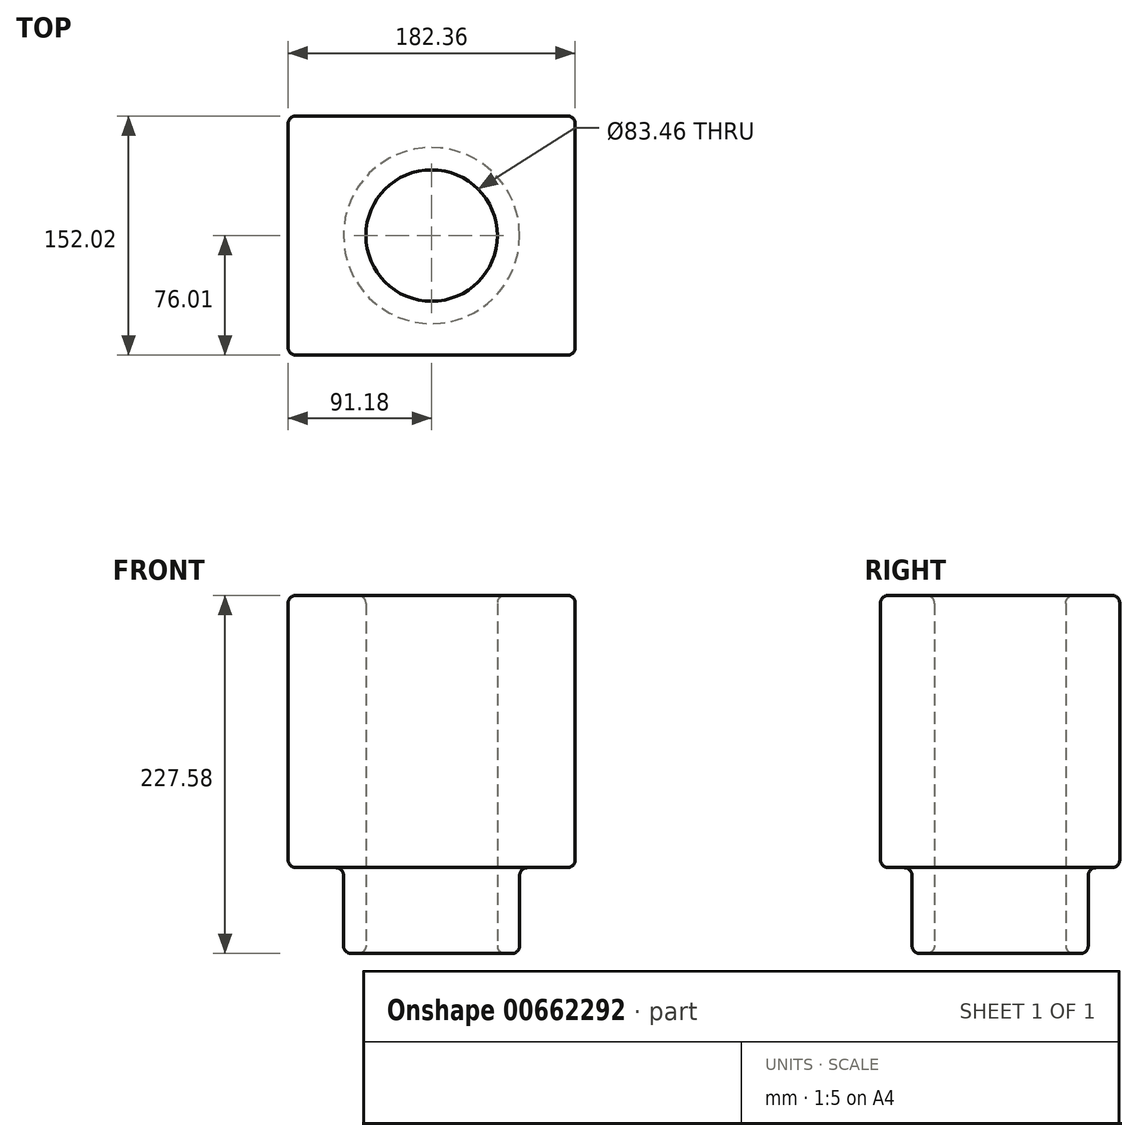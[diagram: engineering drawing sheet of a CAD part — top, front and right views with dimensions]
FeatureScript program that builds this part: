
annotation { "Feature Type Name" : "Feature", "Feature Type Description" : "" }
export const myFeature = defineFeature(function(context is Context, id is Id, definition is map)
    precondition{}
    {
        {
            var Q0;
            Q0=qCreatedBy(makeId("Top.planeOp"),FACE);
            var sketch = newSketch(context, id + "F0", { "sketchPlane" : qUnion([Q0])});
            skLineSegment(sketch, "E0.bottom", {"start": v(-91.18, 76.01) * mm, "end": v(91.18, 76.01) * mm});
            skLineSegment(sketch, "E0.top", {"start": v(-91.18, -76.01) * mm, "end": v(91.18, -76.01) * mm});
            skLineSegment(sketch, "E0.left", {"start": v(-91.18, 76.01) * mm, "end": v(-91.18, -76.01) * mm});
            skLineSegment(sketch, "E0.right", {"start": v(91.18, 76.01) * mm, "end": v(91.18, -76.01) * mm});
            skPoint(sketch, "E0.middle", {"position": v(0, 0) * mm});
            skSolve(sketch);
        }
        {
            var Q0;
            Q0 = qSketchRegion(id + "F0", true);
            extrude(context, id + "F1", {"entities" : qUnion([Q0]), "depth" : 172.97 * mm, "offsetDistance" : 25.4 * mm});
        }
        {
            var Q0;
            Q0=qCreatedBy(makeId("Top.planeOp"),FACE);
            var sketch = newSketch(context, id + "F2", { "sketchPlane" : qUnion([Q0])});
            skCircle(sketch, "E1", {"center": v(0, 0) * mm, "radius": 55.95 * mm});
            skSolve(sketch);
        }
        {
            var Q0;
            Q0=makeQuery(id+"F2.imprint","IMPRINT",FACE,{"disambiguationData":[TD([[makeQuery(id+"F2.imprint","IMPRINT",EDGE,{"derivedFrom":sQuery(id+"F2.wireOp",EDGE,"E1")}),1.0]])]});
            extrude(context, id + "F3", {"entities" : qUnion([Q0]), "operationType" : NewBodyOperationType.ADD, "oppositeDirection" : true, "depth" : 54.6 * mm, "offsetDistance" : 25.4 * mm});
        }
        {
            var Q0;
            Q0=makeQuery(id+"F3.opExtrude","CAP_FACE",FACE,{"disambiguationData":[OSD([sQuery(id+"F2.wireOp",EDGE,"E1")])],"isStart":false});
            var sketch = newSketch(context, id + "F4", { "sketchPlane" : qUnion([Q0])});
            skCircle(sketch, "E2", {"center": v(0, 0) * mm, "radius": 41.73 * mm});
            skSolve(sketch);
        }
        {
            var Q0;
            Q0 = qSketchRegion(id + "F4", true);
            extrude(context, id + "F5", {"entities" : qUnion([Q0]), "operationType" : NewBodyOperationType.REMOVE, "oppositeDirection" : true, "depth" : 271.27 * mm, "offsetDistance" : 25.4 * mm});
        }
        {
            var Q0;
            Q0=makeQuery(id+"F1.opExtrude","SWEPT_FACE",FACE,{"disambiguationData":[OSD([sQuery(id+"F0.wireOp",EDGE,"E0.bottom")])]});
            var Q1;
            Q1=makeQuery(id+"F1.opExtrude","CAP_FACE",FACE,{"disambiguationData":[OSD([sQuery(id+"F0.wireOp",EDGE,"E0.bottom"),sQuery(id+"F0.wireOp",EDGE,"E0.top"),sQuery(id+"F0.wireOp",EDGE,"E0.left"),sQuery(id+"F0.wireOp",EDGE,"E0.right")])],"isStart":true});
            var Q2;
            Q2=makeQuery(id+"F1.opExtrude","SWEPT_FACE",FACE,{"disambiguationData":[OSD([sQuery(id+"F0.wireOp",EDGE,"E0.left")])]});
            var Q3;
            Q3=makeQuery(id+"F3.opExtrude","SWEPT_FACE",FACE,{"disambiguationData":[OSD([sQuery(id+"F2.wireOp",EDGE,"E1")])]});
            var Q4;
            Q4=makeQuery(id+"F5.boolean.opBoolean","COPY",FACE,{"derivedFrom":makeQuery(id+"F5.opExtrude","SWEPT_FACE",FACE,{"disambiguationData":[OSD([sQuery(id+"F4.wireOp",EDGE,"E2")])]})});
            var Q5;
            Q5=makeQuery(id+"F1.opExtrude","CAP_EDGE",EDGE,{"disambiguationData":[OSD([sQuery(id+"F0.wireOp",EDGE,"E0.right")])],"isStart":false});
            var Q6;
            Q6=makeQuery(id+"F1.opExtrude","SWEPT_EDGE",EDGE,{"disambiguationData":[OSD([sQuery(id+"F0.wireOp",EDGE,"E0.top"),sQuery(id+"F0.wireOp",EDGE,"E0.right")])]});
            var Q7;
            Q7=makeQuery(id+"F1.opExtrude","CAP_EDGE",EDGE,{"disambiguationData":[OSD([sQuery(id+"F0.wireOp",EDGE,"E0.top")])],"isStart":false});
            var Q8;
            Q8=makeQuery(id+"F5.boolean.opBoolean","INTERSECT",EDGE,{"derivedFrom":[makeQuery(id+"F1.opExtrude","CAP_FACE",FACE,{"disambiguationData":[OSD([sQuery(id+"F0.wireOp",EDGE,"E0.bottom"),sQuery(id+"F0.wireOp",EDGE,"E0.top"),sQuery(id+"F0.wireOp",EDGE,"E0.left"),sQuery(id+"F0.wireOp",EDGE,"E0.right")])],"isStart":false}),makeQuery(id+"F5.opExtrude","SWEPT_FACE",FACE,{"disambiguationData":[OSD([sQuery(id+"F4.wireOp",EDGE,"E2")])]})]});
            var Q9;
            Q9=makeQuery(id+"F1.opExtrude","CAP_EDGE",EDGE,{"disambiguationData":[OSD([sQuery(id+"F0.wireOp",EDGE,"E0.left")])],"isStart":true});
            var Q10;
            Q10=makeQuery(id+"F1.opExtrude","CAP_EDGE",EDGE,{"disambiguationData":[OSD([sQuery(id+"F0.wireOp",EDGE,"E0.bottom")])],"isStart":false});
            var Q11;
            Q11=makeQuery(id+"F1.opExtrude","CAP_EDGE",EDGE,{"disambiguationData":[OSD([sQuery(id+"F0.wireOp",EDGE,"E0.left")])],"isStart":false});
            var Q12;
            Q12=makeQuery(id+"F1.opExtrude","SWEPT_EDGE",EDGE,{"disambiguationData":[OSD([sQuery(id+"F0.wireOp",EDGE,"E0.top"),sQuery(id+"F0.wireOp",EDGE,"E0.left")])]});
            fillet(context, id + "F6", {"entities" : qUnion([Q0, Q1, Q2, Q3, Q4, Q5, Q6, Q7, Q8, Q9, Q10, Q11, Q12]), "radius" : 5.08 * mm, "tangentPropagation" : true, "allowEdgeOverflow" : false});
        }
    });
